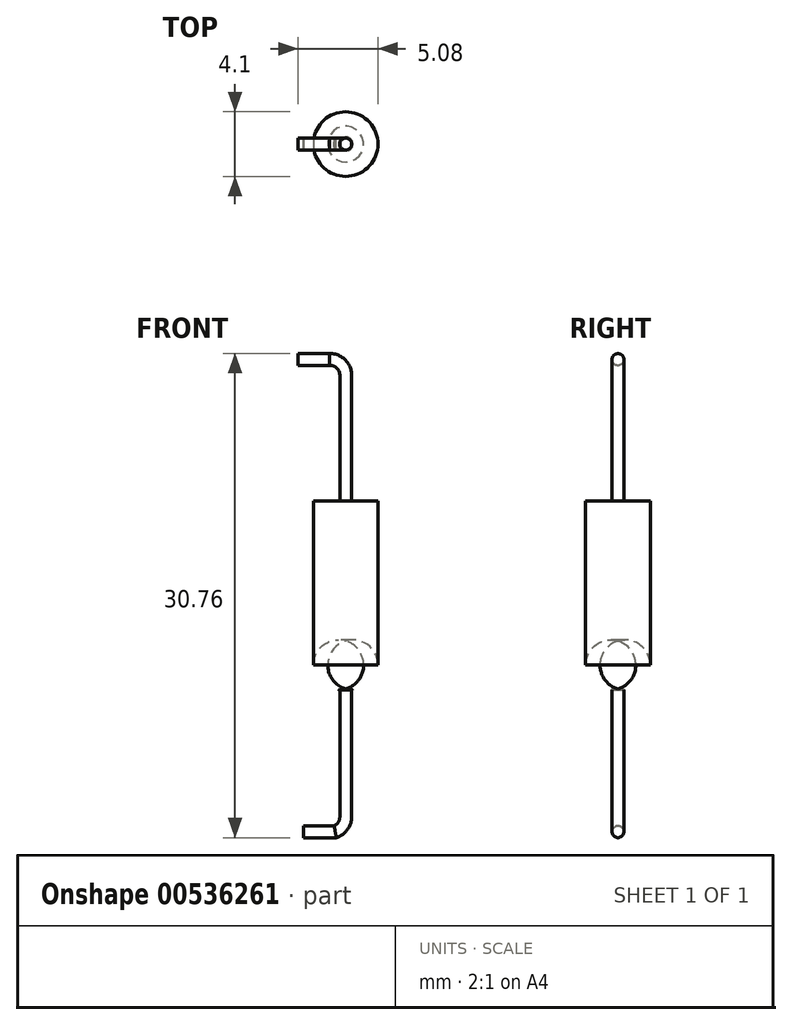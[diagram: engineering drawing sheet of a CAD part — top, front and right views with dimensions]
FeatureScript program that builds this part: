
annotation { "Feature Type Name" : "Feature", "Feature Type Description" : "" }
export const myFeature = defineFeature(function(context is Context, id is Id, definition is map)
    precondition{}
    {
        {
            var Q0;
            Q0=qCreatedBy(makeId("Top.planeOp"),FACE);
            var sketch = newSketch(context, id + "F0", { "sketchPlane" : qUnion([Q0])});
            skCircle(sketch, "E0", {"center": v(0, 0) * mm, "radius": 2.05 * mm});
            skSolve(sketch);
        }
        {
            var Q0;
            Q0 = qSketchRegion(id + "F0", true);
            extrude(context, id + "F1", {"entities" : qUnion([Q0]), "depth" : 12 * mm, "offsetDistance" : 25 * mm});
        }
        {
            var Q0;
            Q0=makeQuery(id+"F1.opExtrude","CAP_FACE",FACE,{"disambiguationData":[OSD([sQuery(id+"F0.wireOp",EDGE,"E0")])],"isStart":true});
            var sketch = newSketch(context, id + "F2", { "sketchPlane" : qUnion([Q0])});
            skCircle(sketch, "E1", {"center": v(0, 0) * mm, "radius": 0.38 * mm});
            skSolve(sketch);
        }
        {
            var Q0;
            Q0=qCreatedBy(makeId("Front.planeOp"),FACE);
            var sketch = newSketch(context, id + "F3", { "sketchPlane" : qUnion([Q0])});
            skLineSegment(sketch, "E2", {"start": v(0, 0) * mm, "end": v(0, -8.06) * mm});
            skArc(sketch, "E3", {"start": v(-0.66, -9) * mm, "mid": v(-0.18, -8.63) * mm, "end": v(0, -8.06) * mm});
            skLineSegment(sketch, "E4", {"start": v(-0.66, -9) * mm, "end": v(-2.66, -9) * mm});
            skSolve(sketch);
        }
        {
            var Q0;
            Q0=makeQuery(id+"F2.imprint","IMPRINT",FACE,{"disambiguationData":[TD([[makeQuery(id+"F2.imprint","IMPRINT",EDGE,{"derivedFrom":sQuery(id+"F2.wireOp",EDGE,"E1")}),1.0]])]});
            var Q1;
            Q1=sQuery(id+"F3.wireOp",EDGE,"E2");
            var Q2;
            Q2=sQuery(id+"F3.wireOp",EDGE,"E3");
            var Q3;
            Q3=sQuery(id+"F3.wireOp",EDGE,"E4");
            sweep(context, id + "F4", {"operationType" : NewBodyOperationType.ADD, "profiles" : qUnion([Q0]), "path" : qUnion([Q1, Q2, Q3])});
        }
        {
            var Q0;
            Q0=makeQuery(id+"F1.opExtrude","CAP_FACE",FACE,{"disambiguationData":[OSD([sQuery(id+"F0.wireOp",EDGE,"E0")])],"isStart":false});
            var sketch = newSketch(context, id + "F5", { "sketchPlane" : qUnion([Q0])});
            skCircle(sketch, "E5", {"center": v(0, 0) * mm, "radius": 0.38 * mm});
            skSolve(sketch);
        }
        {
            var Q0;
            Q0=qCreatedBy(makeId("Front.planeOp"),FACE);
            var sketch = newSketch(context, id + "F6", { "sketchPlane" : qUnion([Q0])});
            skLineSegment(sketch, "E6", {"start": v(0, 12) * mm, "end": v(0, 20) * mm});
            skArc(sketch, "E7", {"start": v(0, 20) * mm, "mid": v(-0.3, 20.72) * mm, "end": v(-1.03, 21) * mm});
            skLineSegment(sketch, "E8", {"start": v(-1.03, 21) * mm, "end": v(-3.03, 21) * mm});
            skSolve(sketch);
        }
        {
            var Q0;
            Q0=makeQuery(id+"F5.imprint","IMPRINT",FACE,{"disambiguationData":[TD([[makeQuery(id+"F5.imprint","IMPRINT",EDGE,{"derivedFrom":sQuery(id+"F5.wireOp",EDGE,"E5")}),1.0]])]});
            var Q1;
            Q1=sQuery(id+"F6.wireOp",EDGE,"E6");
            var Q2;
            Q2=sQuery(id+"F6.wireOp",EDGE,"E7");
            var Q3;
            Q3=sQuery(id+"F6.wireOp",EDGE,"E8");
            sweep(context, id + "F7", {"operationType" : NewBodyOperationType.ADD, "profiles" : qUnion([Q0]), "path" : qUnion([Q1, Q2, Q3])});
        }
        {
            var Q0;
            Q0=makeQuery(id+"F1.opExtrude","CAP_EDGE",EDGE,{"disambiguationData":[OSD([sQuery(id+"F0.wireOp",EDGE,"E0")])],"isStart":true});
            fillet(context, id + "F8", {"entities" : qUnion([Q0]), "radius" : 1.6 * mm, "tangentPropagation" : true, "allowEdgeOverflow" : false});
        }
    });
